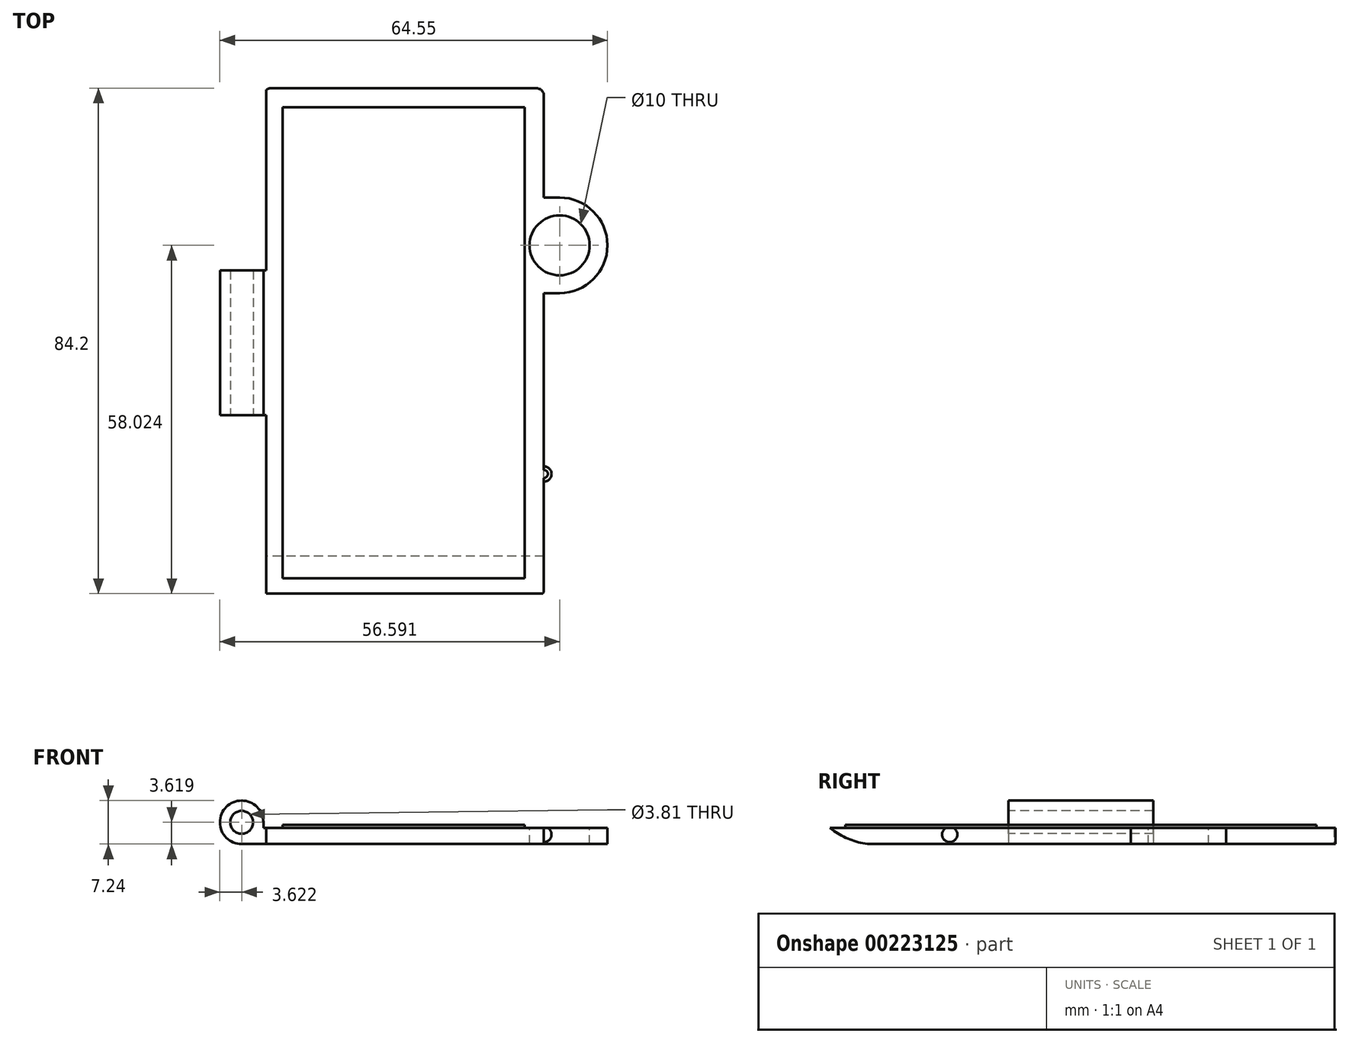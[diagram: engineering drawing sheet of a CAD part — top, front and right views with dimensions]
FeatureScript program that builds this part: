
annotation { "Feature Type Name" : "Feature", "Feature Type Description" : "" }
export const myFeature = defineFeature(function(context is Context, id is Id, definition is map)
    precondition{}
    {
        {
            var Q0;
            Q0=qCreatedBy(makeId("Top.planeOp"),FACE);
            var sketch = newSketch(context, id + "F0", { "sketchPlane" : qUnion([Q0])});
            skLineSegment(sketch, "E0.bottom", {"start": v(22.1, 42.42) * mm, "end": v(-22.1, 42.42) * mm});
            skLineSegment(sketch, "E0.top", {"start": v(22.1, -42.42) * mm, "end": v(-22.1, -42.42) * mm});
            skLineSegment(sketch, "E0.left", {"start": v(23.37, 41.15) * mm, "end": v(23.37, -41.15) * mm});
            skLineSegment(sketch, "E0.right", {"start": v(-23.37, 41.15) * mm, "end": v(-23.37, -41.15) * mm});
            skPoint(sketch, "E0.middle", {"position": v(0, 0) * mm});
            skLineSegment(sketch, "E1.bottom", {"start": v(23.37, 24.2) * mm, "end": v(25.98, 24.2) * mm});
            skLineSegment(sketch, "E1.top", {"start": v(23.37, 8.28) * mm, "end": v(25.98, 8.28) * mm});
            skLineSegment(sketch, "E1.left", {"start": v(23.37, 24.2) * mm, "end": v(23.37, 8.28) * mm});
            skLineSegment(sketch, "E1.right", {"start": v(25.98, 24.2) * mm, "end": v(25.98, 8.28) * mm, "construction": true});
            skArc(sketch, "E2", {"start": v(25.98, 8.28) * mm, "mid": v(33.94, 16.24) * mm, "end": v(25.98, 24.2) * mm});
            skPoint(sketch, "E3.visualSharp", {"position": v(-23.37, 42.42) * mm});
            skArc(sketch, "E3.filletArc", {"start": v(-22.1, 42.42) * mm, "mid": v(-23, 42.05) * mm, "end": v(-23.37, 41.15) * mm});
            skPoint(sketch, "E4.visualSharp", {"position": v(23.37, 42.42) * mm});
            skArc(sketch, "E4.filletArc", {"start": v(23.37, 41.15) * mm, "mid": v(23, 42.05) * mm, "end": v(22.1, 42.42) * mm});
            skPoint(sketch, "E5.visualSharp", {"position": v(23.37, -42.42) * mm});
            skArc(sketch, "E5.filletArc", {"start": v(22.1, -42.42) * mm, "mid": v(23, -42.05) * mm, "end": v(23.37, -41.15) * mm});
            skPoint(sketch, "E6.visualSharp", {"position": v(-23.37, -42.42) * mm});
            skArc(sketch, "E6.filletArc", {"start": v(-23.37, -41.15) * mm, "mid": v(-23, -42.05) * mm, "end": v(-22.1, -42.42) * mm});
            skLineSegment(sketch, "E7", {"start": v(0, 0) * mm, "end": v(0, 16.24) * mm, "construction": true});
            skSolve(sketch);
        }
        {
            var Q0;
            Q0 = qSketchRegion(id + "F0", true);
            extrude(context, id + "F1", {"entities" : qUnion([Q0]), "depth" : 3.17 * mm});
        }
        {
            var Q0;
            Q0=makeQuery(id+"F1.opExtrude","CAP_FACE",FACE,{"disambiguationData":[OSD([sQuery(id+"F0.wireOp",EDGE,"E0.bottom"),sQuery(id+"F0.wireOp",EDGE,"E0.top"),sQuery(id+"F0.wireOp",EDGE,"E0.left"),sQuery(id+"F0.wireOp",EDGE,"E0.right"),sQuery(id+"F0.wireOp",EDGE,"E1.bottom"),sQuery(id+"F0.wireOp",EDGE,"E1.top"),sQuery(id+"F0.wireOp",EDGE,"E2")])],"isStart":false});
            var sketch = newSketch(context, id + "F2", { "sketchPlane" : qUnion([Q0])});
            skCircle(sketch, "E8", {"center": v(25.98, 16.24) * mm, "radius": 5 * mm});
            skSolve(sketch);
        }
        {
            var Q0;
            Q0 = qSketchRegion(id + "F2", true);
            extrude(context, id + "F3", {"entities" : qUnion([Q0]), "operationType" : NewBodyOperationType.REMOVE, "oppositeDirection" : true, "depth" : 3.17 * mm});
        }
        {
            var Q0;
            Q0=makeQuery(id+"F1.opExtrude","CAP_FACE",FACE,{"disambiguationData":[OSD([sQuery(id+"F0.wireOp",EDGE,"E0.bottom"),sQuery(id+"F0.wireOp",EDGE,"E0.top"),sQuery(id+"F0.wireOp",EDGE,"E0.left"),sQuery(id+"F0.wireOp",EDGE,"E0.right"),sQuery(id+"F0.wireOp",EDGE,"E1.bottom"),sQuery(id+"F0.wireOp",EDGE,"E1.top"),sQuery(id+"F0.wireOp",EDGE,"E2")])],"isStart":true});
            var sketch = newSketch(context, id + "F4", { "sketchPlane" : qUnion([Q0])});
            skLineSegment(sketch, "E9.bottom", {"start": v(-23.37, 12.06) * mm, "end": v(-30.6, 12.06) * mm});
            skLineSegment(sketch, "E9.top", {"start": v(-23.37, -12.07) * mm, "end": v(-30.6, -12.07) * mm});
            skLineSegment(sketch, "E9.left", {"start": v(-23.37, 12.06) * mm, "end": v(-23.37, -12.07) * mm});
            skLineSegment(sketch, "E9.right", {"start": v(-30.6, 12.06) * mm, "end": v(-30.6, -12.07) * mm});
            skLineSegment(sketch, "E10", {"start": v(-30.6, 0) * mm, "end": v(-37.76, 0) * mm, "construction": true});
            skSolve(sketch);
        }
        {
            var Q0;
            Q0 = qSketchRegion(id + "F4", true);
            extrude(context, id + "F5", {"entities" : qUnion([Q0]), "operationType" : NewBodyOperationType.ADD, "oppositeDirection" : true, "depth" : 7.24 * mm});
        }
        {
            var Q0;
            Q0=makeQuery(id+"FIdhT0M2mLWxdTl_1.boolean.opBoolean","MERGE",FACE,{"derivedFrom":[makeQuery(id+"F5.opExtrude","SWEPT_FACE",FACE,{"disambiguationData":[OSD([sQuery(id+"F4.wireOp",EDGE,"E9.bottom")])]}),makeQuery(id+"FIdhT0M2mLWxdTl_1.opExtrude","CAP_FACE",FACE,{"disambiguationData":[OSD([sQuery(id+"F73Jyo2bMhZH9Rj_1.wireOp",EDGE,"UTV3WieJ-TXQs-NU0s-NVFI-Aqc4FLV5D8jd"),sQuery(id+"F73Jyo2bMhZH9Rj_1.wireOp",EDGE,"0HvoxmZH-F8q3-QTVT-9co4-aabPweHB1bdE"),sQuery(id+"F73Jyo2bMhZH9Rj_1.wireOp",EDGE,"yNkYTZpz-9iAU-1hEQ-96qI-TEqE45IXLFKw")])],"isStart":true})]});
            var sketch = newSketch(context, id + "F6", { "sketchPlane" : qUnion([Q0])});
            skCircle(sketch, "E11", {"center": v(-26.99, 3.62) * mm, "radius": 1.9 * mm});
            skPoint(sketch, "E11.centerSnap0", {"position": v(-30.6, 3.62) * mm});
            skPoint(sketch, "E11.centerSnap1", {"position": v(-26.99, 7.24) * mm});
            skSolve(sketch);
        }
        {
            var Q0;
            Q0 = qSketchRegion(id + "F6", true);
            extrude(context, id + "F7", {"entities" : qUnion([Q0]), "operationType" : NewBodyOperationType.REMOVE, "oppositeDirection" : true, "depth" : 25.4 * mm});
        }
        {
            var Q0;
            Q0=makeQuery(id+"F5.opExtrude","CAP_EDGE",EDGE,{"disambiguationData":[OSD([sQuery(id+"F4.wireOp",EDGE,"E9.right")])],"isStart":false});
            fillet(context, id + "F8", {"entities" : qUnion([Q0]), "radius" : 3.62 * mm, "tangentPropagation" : true, "allowEdgeOverflow" : false});
        }
        {
            var Q0;
            Q0=makeQuery(id+"F5.opExtrude","CAP_EDGE",EDGE,{"disambiguationData":[OSD([sQuery(id+"F4.wireOp",EDGE,"E9.left")])],"isStart":false});
            fillet(context, id + "F9", {"entities" : qUnion([Q0]), "radius" : 3.62 * mm, "tangentPropagation" : true, "allowEdgeOverflow" : false});
        }
        {
            var Q0;
            Q0=makeQuery(id+"F5.opExtrude","CAP_EDGE",EDGE,{"disambiguationData":[OSD([sQuery(id+"F4.wireOp",EDGE,"E9.right")])],"isStart":true});
            fillet(context, id + "F10", {"entities" : qUnion([Q0]), "radius" : 3.62 * mm, "tangentPropagation" : true, "allowEdgeOverflow" : false});
        }
        {
            var Q0;
            {var subQ0=sQuery(id+"F0.wireOp",EDGE,"E0.left");Q0=makeQuery(id+"F1.opExtrude","SWEPT_FACE",FACE,{"disambiguationData":[OSD([subQ0]),TDD([makeQuery(id+"F0.imprint","IMPRINT",EDGE,{"disambiguationData":[TD([[makeQuery(id+"F0.imprint","INTERSECT",VERTEX,{"derivedFrom":[subQ0,sQuery(id+"F0.wireOp",EDGE,"E5.filletArc")]}),1.0]])],"derivedFrom":subQ0})])]});}
            var sketch = newSketch(context, id + "F11", { "sketchPlane" : qUnion([Q0])});
            skArc(sketch, "E12", {"start": v(-21.86, 0.32) * mm, "mid": v(-20.59, 1.59) * mm, "end": v(-21.86, 2.86) * mm});
            skLineSegment(sketch, "E13", {"start": v(-21.86, 2.86) * mm, "end": v(-21.86, 0.32) * mm});
            skLineSegment(sketch, "E14", {"start": v(-21.86, -2.52) * mm, "end": v(-21.86, 5.4) * mm, "construction": true});
            skSolve(sketch);
        }
        {
            var Q0;
            Q0 = qSketchRegion(id + "F11", true);
            var Q1;
            Q1=sQuery(id+"F11.wireOp",EDGE,"E14");
            revolve(context, id + "F12", {"operationType" : NewBodyOperationType.ADD, "entities" : qUnion([Q0]), "axis" : qUnion([Q1]), "revolveType" : RevolveType.FULL});
        }
        {
            var Q0;
            Q0=makeQuery(id+"F1.opExtrude","CAP_FACE",FACE,{"disambiguationData":[OSD([sQuery(id+"F0.wireOp",EDGE,"E0.bottom"),sQuery(id+"F0.wireOp",EDGE,"E0.top"),sQuery(id+"F0.wireOp",EDGE,"E0.left"),sQuery(id+"F0.wireOp",EDGE,"E0.right"),sQuery(id+"F0.wireOp",EDGE,"E1.bottom"),sQuery(id+"F0.wireOp",EDGE,"E1.top"),sQuery(id+"F0.wireOp",EDGE,"E2"),sQuery(id+"F0.wireOp",EDGE,"E3.filletArc"),sQuery(id+"F0.wireOp",EDGE,"E4.filletArc"),sQuery(id+"F0.wireOp",EDGE,"E5.filletArc"),sQuery(id+"F0.wireOp",EDGE,"E6.filletArc")])],"isStart":false});
            var sketch = newSketch(context, id + "F13", { "sketchPlane" : qUnion([Q0])});
            skLineSegment(sketch, "E15.0", {"start": v(20.2, 39.24) * mm, "end": v(20.2, 22.18) * mm});
            skLineSegment(sketch, "E15.2", {"start": v(20.2, 39.24) * mm, "end": v(-20.2, 39.24) * mm});
            skLineSegment(sketch, "E15.5", {"start": v(20.2, 10.31) * mm, "end": v(20.2, -39.24) * mm});
            skLineSegment(sketch, "E15.6", {"start": v(-20.2, 39.24) * mm, "end": v(-20.2, 12.07) * mm});
            skLineSegment(sketch, "E15.7", {"start": v(-20.2, 12.06) * mm, "end": v(-20.2, -12.06) * mm});
            skLineSegment(sketch, "E15.8", {"start": v(-20.2, -12.06) * mm, "end": v(-20.2, -39.24) * mm});
            skLineSegment(sketch, "E15.9", {"start": v(20.2, -39.24) * mm, "end": v(-20.2, -39.24) * mm});
            skLineSegment(sketch, "E16.0", {"start": v(-23.37, -42.42) * mm, "end": v(23.37, -42.42) * mm});
            skLineSegment(sketch, "E16.1", {"start": v(-23.37, -12.06) * mm, "end": v(-23.37, -42.42) * mm});
            skLineSegment(sketch, "E16.2", {"start": v(23.37, -42.42) * mm, "end": v(23.37, 8.28) * mm});
            skLineSegment(sketch, "E16.3", {"start": v(-23.37, 12.07) * mm, "end": v(-23.37, -12.06) * mm});
            skLineSegment(sketch, "E16.4", {"start": v(-23.37, 42.42) * mm, "end": v(-23.37, 12.07) * mm});
            skLineSegment(sketch, "E16.5", {"start": v(23.37, 42.42) * mm, "end": v(-23.37, 42.42) * mm});
            skLineSegment(sketch, "E16.6", {"start": v(23.37, 8.28) * mm, "end": v(25.98, 8.28) * mm});
            skArc(sketch, "E16.7", {"start": v(25.98, 8.28) * mm, "mid": v(33.94, 16.24) * mm, "end": v(25.98, 24.2) * mm});
            skLineSegment(sketch, "E16.8", {"start": v(25.98, 24.2) * mm, "end": v(23.37, 24.2) * mm});
            skLineSegment(sketch, "E16.9", {"start": v(23.37, 24.2) * mm, "end": v(23.37, 42.42) * mm});
            skLineSegment(sketch, "E17", {"start": v(20.2, 22.18) * mm, "end": v(20.2, 10.31) * mm});
            skLineSegment(sketch, "E18.bottom", {"start": v(23.37, -18.6) * mm, "end": v(26.65, -18.6) * mm});
            skLineSegment(sketch, "E18.top", {"start": v(23.37, -25.35) * mm, "end": v(26.65, -25.35) * mm});
            skLineSegment(sketch, "E18.left", {"start": v(23.37, -18.6) * mm, "end": v(23.37, -25.35) * mm});
            skLineSegment(sketch, "E18.right", {"start": v(26.65, -18.6) * mm, "end": v(26.65, -25.35) * mm});
            skSolve(sketch);
        }
        {
            var Q0;
            Q0 = qSketchRegion(id + "F13", true);
            extrude(context, id + "F14", {"entities" : qUnion([Q0]), "operationType" : NewBodyOperationType.REMOVE, "oppositeDirection" : true, "depth" : 0.5 * mm});
        }
        {
            var Q0;
            {var subQ2=sQuery(id+"F0.wireOp",EDGE,"E3.filletArc");var subQ9=sQuery(id+"F0.wireOp",EDGE,"E0.right");Q0=makeQuery(id+"F5.boolean.opBoolean","SPLIT",FACE,{"disambiguationData":[TD([makeQuery(id+"F1.opExtrude","SWEPT_FACE",FACE,{"disambiguationData":[OSD([subQ2])]})])],"derivedFrom":makeQuery(id+"F1.opExtrude","SWEPT_FACE",FACE,{"disambiguationData":[OSD([subQ9])]})});}
            var sketch = newSketch(context, id + "F15", { "sketchPlane" : qUnion([Q0])});
            skLineSegment(sketch, "E19.bottom", {"start": v(-42.42, 2.68) * mm, "end": v(-12.06, 2.68) * mm});
            skLineSegment(sketch, "E19.top", {"start": v(-42.42, 0) * mm, "end": v(-12.06, 0) * mm});
            skLineSegment(sketch, "E19.left", {"start": v(-42.42, 2.68) * mm, "end": v(-42.42, 0) * mm});
            skLineSegment(sketch, "E19.right", {"start": v(-12.06, 2.68) * mm, "end": v(-12.06, 0) * mm});
            skLineSegment(sketch, "E20.bottom", {"start": v(12.06, 2.68) * mm, "end": v(42.42, 2.68) * mm});
            skLineSegment(sketch, "E20.top", {"start": v(12.06, 0) * mm, "end": v(42.42, 0) * mm});
            skLineSegment(sketch, "E20.left", {"start": v(12.07, 2.68) * mm, "end": v(12.07, 0) * mm});
            skLineSegment(sketch, "E20.right", {"start": v(42.42, 2.68) * mm, "end": v(42.42, 0) * mm});
            skSolve(sketch);
        }
        {
            var Q0;
            Q0 = qSketchRegion(id + "F15", true);
            extrude(context, id + "F16", {"entities" : qUnion([Q0]), "operationType" : NewBodyOperationType.REMOVE, "oppositeDirection" : true, "depth" : 0.5 * mm});
        }
        {
            var Q0;
            Q0=makeQuery(id+"F16.boolean.opBoolean","COPY",FACE,{"derivedFrom":makeQuery(id+"F16.opExtrude","CAP_FACE",FACE,{"disambiguationData":[OSD([sQuery(id+"F15.wireOp",EDGE,"E20.bottom"),sQuery(id+"F15.wireOp",EDGE,"E20.top"),sQuery(id+"F15.wireOp",EDGE,"E20.left"),sQuery(id+"F15.wireOp",EDGE,"E20.right")])],"isStart":false})});
            var sketch = newSketch(context, id + "F17", { "sketchPlane" : qUnion([Q0])});
            skLineSegment(sketch, "E21.bottom", {"start": v(42.42, 0) * mm, "end": v(44, 0) * mm, "construction": true});
            skLineSegment(sketch, "E21.top", {"start": v(42.42, 2.68) * mm, "end": v(44, 2.68) * mm, "construction": true});
            skLineSegment(sketch, "E21.left", {"start": v(42.42, 0) * mm, "end": v(42.42, 2.68) * mm, "construction": true});
            skLineSegment(sketch, "E21.right", {"start": v(44, 0) * mm, "end": v(44, 2.68) * mm, "construction": true});
            skArc(sketch, "E22", {"start": v(35.56, 0) * mm, "mid": v(40.28, 1.64) * mm, "end": v(44, 4.97) * mm});
            skLineSegment(sketch, "E23", {"start": v(44, 0) * mm, "end": v(35.56, 0) * mm});
            skLineSegment(sketch, "E24", {"start": v(44, 0) * mm, "end": v(44, 4.97) * mm});
            skPoint(sketch, "E24.endSnap0", {"position": v(44, 1.34) * mm});
            skSolve(sketch);
        }
        {
            var Q0;
            Q0 = qSketchRegion(id + "F17", true);
            var Q1;
            {var subQ0=sQuery(id+"F0.wireOp",EDGE,"E0.left");Q1=makeQuery(id+"F1.opExtrude","SWEPT_FACE",FACE,{"disambiguationData":[OSD([subQ0]),TDD([makeQuery(id+"F0.imprint","IMPRINT",EDGE,{"disambiguationData":[TD([[makeQuery(id+"F0.imprint","INTERSECT",VERTEX,{"derivedFrom":[subQ0,sQuery(id+"F0.wireOp",EDGE,"E5.filletArc")]}),1.0]])],"derivedFrom":subQ0})])]});}
            extrude(context, id + "F18", {"entities" : qUnion([Q0]), "operationType" : NewBodyOperationType.REMOVE, "endBound" : BoundingType.UP_TO_SURFACE, "oppositeDirection" : true, "endBoundEntityFace" : qUnion([Q1]), "depth" : 25.4 * mm});
        }
    });
